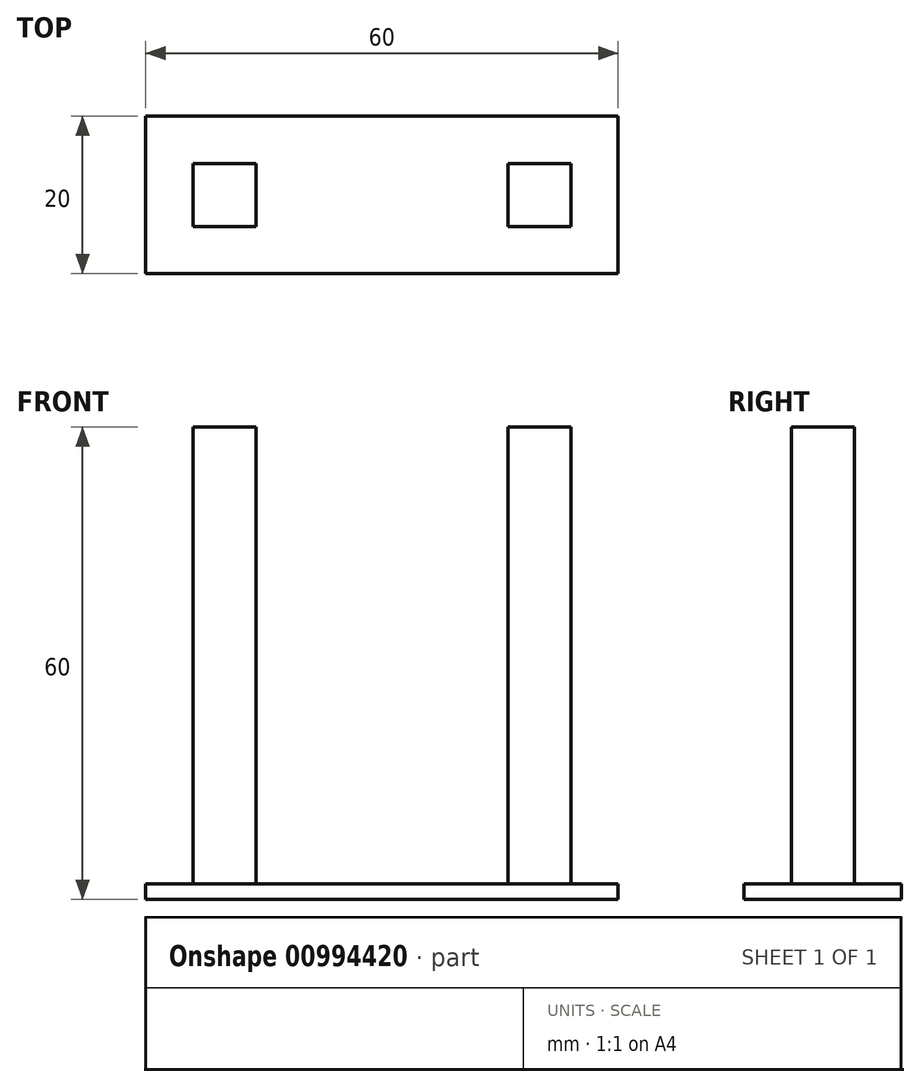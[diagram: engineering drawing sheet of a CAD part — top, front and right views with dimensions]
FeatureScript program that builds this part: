
annotation { "Feature Type Name" : "Feature", "Feature Type Description" : "" }
export const myFeature = defineFeature(function(context is Context, id is Id, definition is map)
    precondition{}
    {
        {
            var Q0;
            Q0=qCreatedBy(makeId("Top.planeOp"),FACE);
            var sketch = newSketch(context, id + "F0", { "sketchPlane" : qUnion([Q0])});
            skLineSegment(sketch, "E0.bottom", {"start": v(30, 10) * mm, "end": v(-30, 10) * mm});
            skLineSegment(sketch, "E0.top", {"start": v(30, -10) * mm, "end": v(-30, -10) * mm});
            skLineSegment(sketch, "E0.left", {"start": v(30, 10) * mm, "end": v(30, -10) * mm});
            skLineSegment(sketch, "E0.right", {"start": v(-30, 10) * mm, "end": v(-30, -10) * mm});
            skPoint(sketch, "E0.middle", {"position": v(0, 0) * mm});
            skLineSegment(sketch, "E1", {"start": v(0, 0) * mm, "end": v(-20, 0) * mm, "construction": true});
            skLineSegment(sketch, "E2.bottom", {"start": v(-15, 5) * mm, "end": v(-25, 5) * mm});
            skLineSegment(sketch, "E2.top", {"start": v(-15, -5) * mm, "end": v(-25, -5) * mm});
            skLineSegment(sketch, "E2.left", {"start": v(-15, 5) * mm, "end": v(-15, -5) * mm});
            skLineSegment(sketch, "E2.right", {"start": v(-25, 5) * mm, "end": v(-25, -5) * mm});
            skPoint(sketch, "E2.middle", {"position": v(-20, 0) * mm});
            skLineSegment(sketch, "E3", {"start": v(0, 0) * mm, "end": v(0, 4.45) * mm, "construction": true});
            skLineSegment(sketch, "E4.0", {"start": v(-16, 4) * mm, "end": v(-24, 4) * mm});
            skLineSegment(sketch, "E4.1", {"start": v(-16, 4) * mm, "end": v(-16, -4) * mm});
            skLineSegment(sketch, "E4.2", {"start": v(-16, -4) * mm, "end": v(-24, -4) * mm});
            skLineSegment(sketch, "E4.3", {"start": v(-24, 4) * mm, "end": v(-24, -4) * mm});
            skLineSegment(sketch, "E5.MirrorCS", {"start": v(-16, -4) * mm, "end": v(-16, 4) * mm});
            skLineSegment(sketch, "E6.MirrorCS", {"start": v(-25, -5) * mm, "end": v(-25, 5) * mm});
            skLineSegment(sketch, "E7.MirrorCS", {"start": v(-15, -5) * mm, "end": v(-15, 5) * mm});
            skLineSegment(sketch, "E8.MirrorCS", {"start": v(-24, -4) * mm, "end": v(-24, 4) * mm});
            skPoint(sketch, "E9.MirrorP", {"position": v(20, 0) * mm});
            skLineSegment(sketch, "E10.MirrorCS", {"start": v(25, 5) * mm, "end": v(25, -5) * mm});
            skLineSegment(sketch, "E11.MirrorCS", {"start": v(16, -4) * mm, "end": v(16, 4) * mm});
            skLineSegment(sketch, "E12.MirrorCS", {"start": v(15, -5) * mm, "end": v(25, -5) * mm});
            skLineSegment(sketch, "E13.MirrorCS", {"start": v(15, 5) * mm, "end": v(15, -5) * mm});
            skLineSegment(sketch, "E14.MirrorCS", {"start": v(16, -4) * mm, "end": v(24, -4) * mm});
            skLineSegment(sketch, "E15.MirrorCS", {"start": v(24, -4) * mm, "end": v(24, 4) * mm});
            skLineSegment(sketch, "E16.MirrorCS", {"start": v(15, 5) * mm, "end": v(25, 5) * mm});
            skLineSegment(sketch, "E17.MirrorCS", {"start": v(16, 4) * mm, "end": v(24, 4) * mm});
            skLineSegment(sketch, "E18.MirrorCS", {"start": v(16, 4) * mm, "end": v(16, -4) * mm});
            skLineSegment(sketch, "E19.MirrorCS", {"start": v(15, -5) * mm, "end": v(15, 5) * mm});
            skLineSegment(sketch, "E20.MirrorCS", {"start": v(24, 4) * mm, "end": v(24, -4) * mm});
            skLineSegment(sketch, "E21.MirrorCS", {"start": v(0, 0) * mm, "end": v(20, 0) * mm, "construction": true});
            skLineSegment(sketch, "E22.MirrorCS", {"start": v(25, -5) * mm, "end": v(25, 5) * mm});
            skLineSegment(sketch, "E23.bottom", {"start": v(15, 2.5) * mm, "end": v(-15, 2.5) * mm});
            skLineSegment(sketch, "E23.top", {"start": v(15, -2.5) * mm, "end": v(-15, -2.5) * mm});
            skLineSegment(sketch, "E23.left", {"start": v(15, 2.5) * mm, "end": v(15, -2.5) * mm});
            skLineSegment(sketch, "E23.right", {"start": v(-15, 2.5) * mm, "end": v(-15, -2.5) * mm});
            skSolve(sketch);
        }
        {
            var Q0;
            Q0=makeQuery(id+"F0.imprint","IMPRINT",FACE,{"disambiguationData":[TD([[makeQuery(id+"F0.imprint","IMPRINT",EDGE,{"derivedFrom":sQuery(id+"F0.wireOp",EDGE,"E4.0")}),1.0]])]});
            var Q1;
            {var subQ0=sQuery(id+"F0.wireOp",EDGE,"E23.bottom");Q1=makeQuery(id+"F0.imprint","IMPRINT",FACE,{"disambiguationData":[TD([[makeQuery(id+"F0.imprint","IMPRINT",EDGE,{"derivedFrom":subQ0}),1.0]])]});}
            var Q2;
            {var subQ4=sQuery(id+"F0.wireOp",EDGE,"E2.bottom");Q2=makeQuery(id+"F0.imprint","IMPRINT",FACE,{"disambiguationData":[TD([[makeQuery(id+"F0.imprint","IMPRINT",EDGE,{"derivedFrom":subQ4}),1.0]])]});}
            var Q3;
            Q3=makeQuery(id+"F0.imprint","IMPRINT",FACE,{"disambiguationData":[TD([[makeQuery(id+"F0.imprint","IMPRINT",EDGE,{"derivedFrom":sQuery(id+"F0.wireOp",EDGE,"E0.bottom")}),1.0]])]});
            var Q4;
            Q4=makeQuery(id+"F0.imprint","IMPRINT",FACE,{"disambiguationData":[TD([[makeQuery(id+"F0.imprint","IMPRINT",EDGE,{"derivedFrom":sQuery(id+"F0.wireOp",EDGE,"E10.MirrorCS")}),-1.0]])]});
            var Q5;
            Q5=makeQuery(id+"F0.imprint","IMPRINT",FACE,{"disambiguationData":[TD([[makeQuery(id+"F0.imprint","IMPRINT",EDGE,{"derivedFrom":sQuery(id+"F0.wireOp",EDGE,"E11.MirrorCS")}),-1.0]])]});
            extrude(context, id + "F1", {"entities" : qUnion([Q0, Q1, Q2, Q3, Q4, Q5]), "depth" : 2 * mm, "offsetDistance" : 25 * mm});
        }
        {
            var Q0;
            Q0=makeQuery(id+"F0.imprint","IMPRINT",FACE,{"disambiguationData":[TD([[makeQuery(id+"F0.imprint","IMPRINT",EDGE,{"derivedFrom":sQuery(id+"F0.wireOp",EDGE,"E4.0")}),1.0]])]});
            var Q1;
            Q1=makeQuery(id+"F0.imprint","IMPRINT",FACE,{"disambiguationData":[TD([[makeQuery(id+"F0.imprint","IMPRINT",EDGE,{"derivedFrom":sQuery(id+"F0.wireOp",EDGE,"E11.MirrorCS")}),-1.0]])]});
            extrude(context, id + "F2", {"entities" : qUnion([Q0, Q1]), "operationType" : NewBodyOperationType.ADD, "depth" : 60 * mm, "offsetDistance" : 25 * mm});
        }
    });
